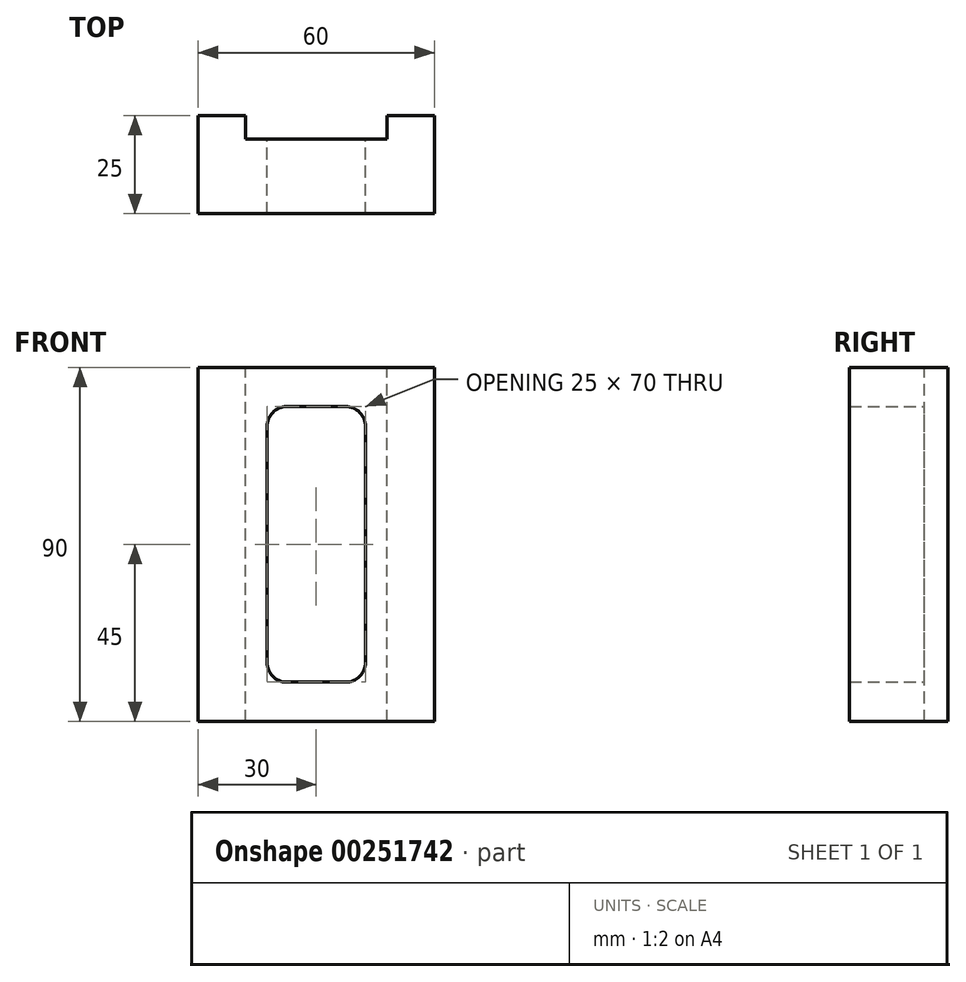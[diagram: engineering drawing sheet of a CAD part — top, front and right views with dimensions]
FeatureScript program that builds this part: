
annotation { "Feature Type Name" : "Feature", "Feature Type Description" : "" }
export const myFeature = defineFeature(function(context is Context, id is Id, definition is map)
    precondition{}
    {
        {
            var Q0;
            Q0=qCreatedBy(makeId("Front.planeOp"),FACE);
            var sketch = newSketch(context, id + "F0", { "sketchPlane" : qUnion([Q0])});
            skLineSegment(sketch, "E0.bottom", {"start": v(30, -45) * mm, "end": v(-30, -45) * mm});
            skLineSegment(sketch, "E0.top", {"start": v(30, 45) * mm, "end": v(-30, 45) * mm});
            skLineSegment(sketch, "E0.left", {"start": v(30, -45) * mm, "end": v(30, 45) * mm});
            skLineSegment(sketch, "E0.right", {"start": v(-30, -45) * mm, "end": v(-30, 45) * mm});
            skPoint(sketch, "E0.middle", {"position": v(0, 0) * mm});
            skLineSegment(sketch, "E1.bottom", {"start": v(12.5, -35) * mm, "end": v(-12.5, -35) * mm});
            skLineSegment(sketch, "E1.top", {"start": v(12.5, 35) * mm, "end": v(-12.5, 35) * mm});
            skLineSegment(sketch, "E1.left", {"start": v(12.5, -35) * mm, "end": v(12.5, 35) * mm});
            skLineSegment(sketch, "E1.right", {"start": v(-12.5, -35) * mm, "end": v(-12.5, 35) * mm});
            skSolve(sketch);
        }
        {
            var Q0;
            Q0 = qSketchRegion(id + "F0", true);
            extrude(context, id + "F1", {"entities" : qUnion([Q0]), "endBound" : BoundingType.SYMMETRIC, "depth" : 25 * mm, "offsetDistance" : 25 * mm});
        }
        {
            var Q0;
            Q0=makeQuery(id+"F1.opExtrude","SWEPT_FACE",FACE,{"disambiguationData":[OSD([sQuery(id+"F0.wireOp",EDGE,"E0.top")])]});
            var sketch = newSketch(context, id + "F2", { "sketchPlane" : qUnion([Q0])});
            skLineSegment(sketch, "E2.bottom", {"start": v(-18, 12.5) * mm, "end": v(18, 12.5) * mm});
            skLineSegment(sketch, "E2.top", {"start": v(-18, 6.5) * mm, "end": v(18, 6.5) * mm});
            skLineSegment(sketch, "E2.left", {"start": v(-18, 12.5) * mm, "end": v(-18, 6.5) * mm});
            skLineSegment(sketch, "E2.right", {"start": v(18, 12.5) * mm, "end": v(18, 6.5) * mm});
            skSolve(sketch);
        }
        {
            var Q0;
            Q0 = qSketchRegion(id + "F2", true);
            extrude(context, id + "F3", {"entities" : qUnion([Q0]), "operationType" : NewBodyOperationType.REMOVE, "endBound" : BoundingType.THROUGH_ALL, "oppositeDirection" : true, "depth" : 25 * mm, "offsetDistance" : 25 * mm});
        }
        {
            var Q0;
            Q0=makeQuery(id+"F1.opExtrude","SWEPT_EDGE",EDGE,{"disambiguationData":[OSD([sQuery(id+"F0.wireOp",EDGE,"E1.top"),sQuery(id+"F0.wireOp",EDGE,"E1.right")])]});
            var Q1;
            Q1=makeQuery(id+"F1.opExtrude","SWEPT_EDGE",EDGE,{"disambiguationData":[OSD([sQuery(id+"F0.wireOp",EDGE,"E1.top"),sQuery(id+"F0.wireOp",EDGE,"E1.left")])]});
            var Q2;
            Q2=makeQuery(id+"F1.opExtrude","SWEPT_EDGE",EDGE,{"disambiguationData":[OSD([sQuery(id+"F0.wireOp",EDGE,"E1.bottom"),sQuery(id+"F0.wireOp",EDGE,"E1.left")])]});
            var Q3;
            Q3=makeQuery(id+"F1.opExtrude","SWEPT_EDGE",EDGE,{"disambiguationData":[OSD([sQuery(id+"F0.wireOp",EDGE,"E1.bottom"),sQuery(id+"F0.wireOp",EDGE,"E1.right")])]});
            fillet(context, id + "F4", {"entities" : qUnion([Q0, Q1, Q2, Q3]), "radius" : 5 * mm, "tangentPropagation" : true, "allowEdgeOverflow" : false});
        }
    });
